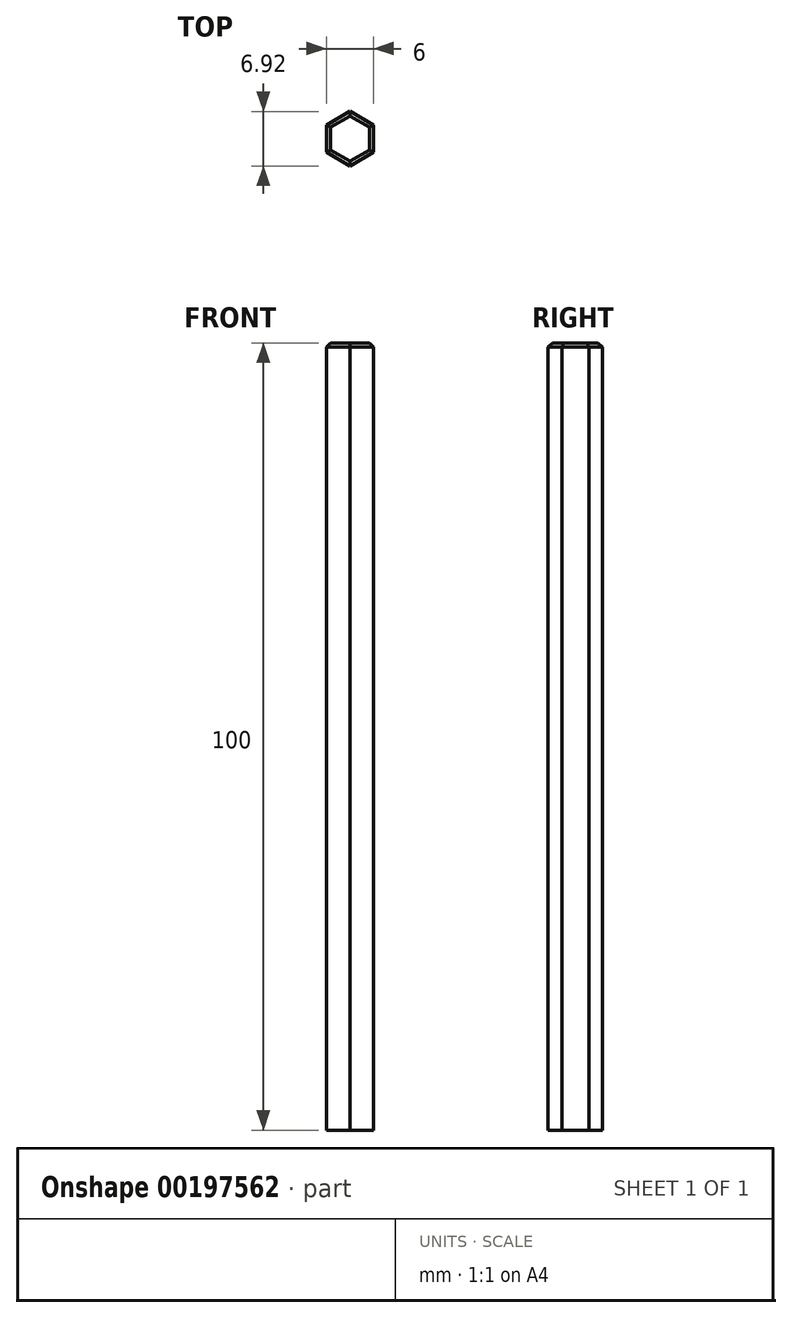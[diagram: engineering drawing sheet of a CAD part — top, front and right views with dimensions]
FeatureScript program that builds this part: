
annotation { "Feature Type Name" : "Feature", "Feature Type Description" : "" }
export const myFeature = defineFeature(function(context is Context, id is Id, definition is map)
    precondition{}
    {
        {
            var Q0;
            Q0=qCreatedBy(makeId("Top.planeOp"),FACE);
            var sketch = newSketch(context, id + "F0", { "sketchPlane" : qUnion([Q0])});
            skCircle(sketch, "E0.cCircle", {"center": v(0, 0) * mm, "radius": 3 * mm, "construction": true});
            skLineSegment(sketch, "E0.0", {"start": v(3, 1.73) * mm, "end": v(3, -1.73) * mm});
            skLineSegment(sketch, "E0.1", {"start": v(3, -1.73) * mm, "end": v(0, -3.46) * mm});
            skLineSegment(sketch, "E0.2", {"start": v(0, -3.46) * mm, "end": v(-3, -1.73) * mm});
            skLineSegment(sketch, "E0.3", {"start": v(-3, -1.73) * mm, "end": v(-3, 1.73) * mm});
            skLineSegment(sketch, "E0.4", {"start": v(-3, 1.73) * mm, "end": v(0, 3.46) * mm});
            skLineSegment(sketch, "E0.5", {"start": v(0, 3.46) * mm, "end": v(3, 1.73) * mm});
            skPoint(sketch, "E0.0.midPoint", {"position": v(3, 0) * mm});
            skSolve(sketch);
        }
        {
            var Q0;
            Q0=makeQuery(id+"F0.imprint","IMPRINT",FACE,{"disambiguationData":[TD([[makeQuery(id+"F0.imprint","IMPRINT",EDGE,{"derivedFrom":sQuery(id+"F0.wireOp",EDGE,"E0.0")}),-1.0]])]});
            extrude(context, id + "F1", {"entities" : qUnion([Q0]), "depth" : 100 * mm});
        }
        {
            var Q0;
            Q0=makeQuery(id+"F1.opExtrude","CAP_FACE",FACE,{"disambiguationData":[OSD([sQuery(id+"F0.wireOp",EDGE,"E0.0"),sQuery(id+"F0.wireOp",EDGE,"E0.1"),sQuery(id+"F0.wireOp",EDGE,"E0.2"),sQuery(id+"F0.wireOp",EDGE,"E0.3"),sQuery(id+"F0.wireOp",EDGE,"E0.4"),sQuery(id+"F0.wireOp",EDGE,"E0.5")])],"isStart":false});
            chamfer(context, id + "F2", {"entities" : qUnion([Q0]), "width" : .5 * mm, "tangentPropagation" : true});
        }
    });
